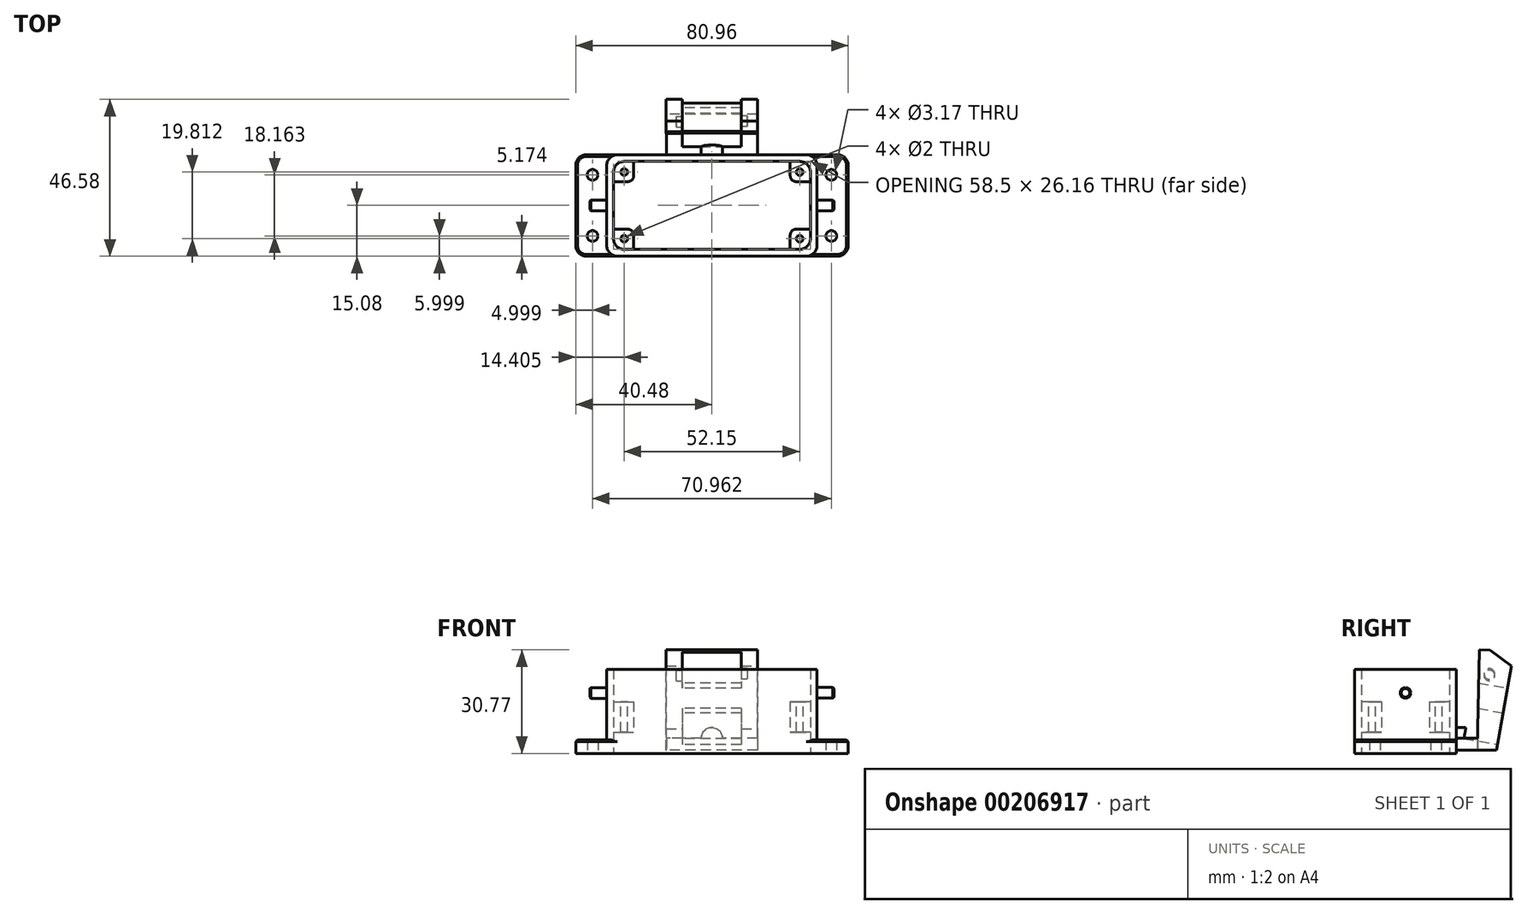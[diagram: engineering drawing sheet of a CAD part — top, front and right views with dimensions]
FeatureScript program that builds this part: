
annotation { "Feature Type Name" : "Feature", "Feature Type Description" : "" }
export const myFeature = defineFeature(function(context is Context, id is Id, definition is map)
    precondition{}
    {
        {
            var Q0;
            Q0=qCreatedBy(makeId("Top.planeOp"),FACE);
            var sketch = newSketch(context, id + "F0", { "sketchPlane" : qUnion([Q0])});
            skLineSegment(sketch, "E0.bottom", {"start": v(-37.3, 15.08) * mm, "end": v(37.3, 15.08) * mm});
            skLineSegment(sketch, "E0.top", {"start": v(-37.3, -15.08) * mm, "end": v(37.3, -15.08) * mm});
            skLineSegment(sketch, "E0.left", {"start": v(-40.48, 11.9) * mm, "end": v(-40.48, -11.9) * mm});
            skLineSegment(sketch, "E0.right", {"start": v(40.48, 11.9) * mm, "end": v(40.48, -11.9) * mm});
            skPoint(sketch, "E0.middle", {"position": v(0, 0) * mm});
            skCircle(sketch, "E1", {"center": v(-35.48, 9.08) * mm, "radius": 1.59 * mm});
            skCircle(sketch, "E2", {"center": v(-35.48, -9.08) * mm, "radius": 1.59 * mm});
            skCircle(sketch, "E3", {"center": v(35.48, -9.08) * mm, "radius": 1.59 * mm});
            skCircle(sketch, "E4", {"center": v(35.48, 9.08) * mm, "radius": 1.59 * mm});
            skPoint(sketch, "E5.visualSharp", {"position": v(-40.48, 15.08) * mm});
            skArc(sketch, "E5.filletArc", {"start": v(-37.3, 15.08) * mm, "mid": v(-39.55, 14.15) * mm, "end": v(-40.48, 11.9) * mm});
            skPoint(sketch, "E6.visualSharp", {"position": v(-40.48, -15.08) * mm});
            skArc(sketch, "E6.filletArc", {"start": v(-40.48, -11.9) * mm, "mid": v(-39.55, -14.15) * mm, "end": v(-37.3, -15.08) * mm});
            skPoint(sketch, "E7.visualSharp", {"position": v(40.48, -15.08) * mm});
            skArc(sketch, "E7.filletArc", {"start": v(37.3, -15.08) * mm, "mid": v(39.55, -14.15) * mm, "end": v(40.48, -11.9) * mm});
            skPoint(sketch, "E8.visualSharp", {"position": v(40.48, 15.08) * mm});
            skArc(sketch, "E8.filletArc", {"start": v(40.48, 11.9) * mm, "mid": v(39.55, 14.15) * mm, "end": v(37.3, 15.08) * mm});
            skLineSegment(sketch, "E9.bottom", {"start": v(-26.07, 13.08) * mm, "end": v(26.07, 13.08) * mm});
            skLineSegment(sketch, "E9.top", {"start": v(-26.07, -13.08) * mm, "end": v(26.07, -13.08) * mm});
            skLineSegment(sketch, "E9.left", {"start": v(-29.25, 9.9) * mm, "end": v(-29.25, -9.9) * mm});
            skLineSegment(sketch, "E9.right", {"start": v(29.25, 9.9) * mm, "end": v(29.25, -9.9) * mm});
            skPoint(sketch, "E10.visualSharp", {"position": v(-29.25, 13.08) * mm});
            skArc(sketch, "E10.filletArc", {"start": v(-26.07, 13.08) * mm, "mid": v(-28.32, 12.15) * mm, "end": v(-29.25, 9.9) * mm});
            skPoint(sketch, "E11.visualSharp", {"position": v(-29.25, -13.08) * mm});
            skArc(sketch, "E11.filletArc", {"start": v(-29.25, -9.9) * mm, "mid": v(-28.32, -12.15) * mm, "end": v(-26.07, -13.08) * mm});
            skPoint(sketch, "E12.visualSharp", {"position": v(29.25, -13.08) * mm});
            skArc(sketch, "E12.filletArc", {"start": v(26.07, -13.08) * mm, "mid": v(28.32, -12.15) * mm, "end": v(29.25, -9.9) * mm});
            skPoint(sketch, "E13.visualSharp", {"position": v(29.25, 13.08) * mm});
            skArc(sketch, "E13.filletArc", {"start": v(29.25, 9.9) * mm, "mid": v(28.32, 12.15) * mm, "end": v(26.07, 13.08) * mm});
            skSolve(sketch);
        }
        {
            var Q0;
            Q0=qSketchRegion(id+"F0",true);
            extrude(context, id + "F1", {"entities" : qUnion([Q0]), "depth" : 4 * mm});
        }
        {
            var Q0;
            Q0=makeQuery(id+"F1.opExtrude","CAP_FACE",FACE,{"disambiguationData":[OSD([sQuery(id+"F0.wireOp",EDGE,"E0.bottom"),sQuery(id+"F0.wireOp",EDGE,"E0.top"),sQuery(id+"F0.wireOp",EDGE,"E0.left"),sQuery(id+"F0.wireOp",EDGE,"E0.right"),sQuery(id+"F0.wireOp",EDGE,"E1"),sQuery(id+"F0.wireOp",EDGE,"E2"),sQuery(id+"F0.wireOp",EDGE,"E3"),sQuery(id+"F0.wireOp",EDGE,"E4"),sQuery(id+"F0.wireOp",EDGE,"E5.filletArc"),sQuery(id+"F0.wireOp",EDGE,"E6.filletArc"),sQuery(id+"F0.wireOp",EDGE,"E7.filletArc"),sQuery(id+"F0.wireOp",EDGE,"E8.filletArc"),sQuery(id+"F0.wireOp",EDGE,"E9.bottom"),sQuery(id+"F0.wireOp",EDGE,"E9.top"),sQuery(id+"F0.wireOp",EDGE,"E9.left"),sQuery(id+"F0.wireOp",EDGE,"E9.right"),sQuery(id+"F0.wireOp",EDGE,"E10.filletArc"),sQuery(id+"F0.wireOp",EDGE,"E11.filletArc"),sQuery(id+"F0.wireOp",EDGE,"E12.filletArc"),sQuery(id+"F0.wireOp",EDGE,"E13.filletArc")])],"isStart":false});
            var sketch = newSketch(context, id + "F2", { "sketchPlane" : qUnion([Q0])});
            skLineSegment(sketch, "E14.bottom", {"start": v(-26.07, 13.08) * mm, "end": v(26.07, 13.08) * mm});
            skLineSegment(sketch, "E14.top", {"start": v(-26.07, -13.08) * mm, "end": v(26.07, -13.08) * mm});
            skLineSegment(sketch, "E14.left", {"start": v(-29.25, 9.9) * mm, "end": v(-29.25, -9.9) * mm});
            skLineSegment(sketch, "E14.right", {"start": v(29.25, 9.9) * mm, "end": v(29.25, -9.9) * mm});
            skPoint(sketch, "E14.middle", {"position": v(0, 0) * mm});
            skPoint(sketch, "E15.visualSharp", {"position": v(-29.25, 13.08) * mm});
            skArc(sketch, "E15.filletArc", {"start": v(-26.07, 13.08) * mm, "mid": v(-28.32, 12.15) * mm, "end": v(-29.25, 9.9) * mm});
            skPoint(sketch, "E16.visualSharp", {"position": v(-29.25, -13.08) * mm});
            skArc(sketch, "E16.filletArc", {"start": v(-29.25, -9.9) * mm, "mid": v(-28.32, -12.15) * mm, "end": v(-26.07, -13.08) * mm});
            skPoint(sketch, "E17.visualSharp", {"position": v(29.25, -13.08) * mm});
            skArc(sketch, "E17.filletArc", {"start": v(26.07, -13.08) * mm, "mid": v(28.32, -12.15) * mm, "end": v(29.25, -9.9) * mm});
            skPoint(sketch, "E18.visualSharp", {"position": v(29.25, 13.08) * mm});
            skArc(sketch, "E18.filletArc", {"start": v(29.25, 9.9) * mm, "mid": v(28.32, 12.15) * mm, "end": v(26.07, 13.08) * mm});
            skLineSegment(sketch, "E19.bottom", {"start": v(-28.08, 15.08) * mm, "end": v(28.08, 15.08) * mm});
            skLineSegment(sketch, "E19.top", {"start": v(-28.08, -15.08) * mm, "end": v(28.08, -15.08) * mm});
            skLineSegment(sketch, "E19.left", {"start": v(-31.25, 11.9) * mm, "end": v(-31.25, -11.9) * mm});
            skLineSegment(sketch, "E19.right", {"start": v(31.25, 11.9) * mm, "end": v(31.25, -11.9) * mm});
            skPoint(sketch, "E20.visualSharp", {"position": v(-31.25, 15.08) * mm});
            skArc(sketch, "E20.filletArc", {"start": v(-28.08, 15.08) * mm, "mid": v(-30.32, 14.15) * mm, "end": v(-31.25, 11.9) * mm});
            skPoint(sketch, "E21.visualSharp", {"position": v(-31.25, -15.08) * mm});
            skArc(sketch, "E21.filletArc", {"start": v(-31.25, -11.9) * mm, "mid": v(-30.32, -14.15) * mm, "end": v(-28.08, -15.08) * mm});
            skPoint(sketch, "E22.visualSharp", {"position": v(31.25, -15.08) * mm});
            skArc(sketch, "E22.filletArc", {"start": v(28.08, -15.08) * mm, "mid": v(30.32, -14.15) * mm, "end": v(31.25, -11.9) * mm});
            skPoint(sketch, "E23.visualSharp", {"position": v(31.25, 15.08) * mm});
            skArc(sketch, "E23.filletArc", {"start": v(31.25, 11.9) * mm, "mid": v(30.32, 14.15) * mm, "end": v(28.08, 15.08) * mm});
            skSolve(sketch);
        }
        {
            var Q0;
            Q0=qSketchRegion(id+"F2",true);
            extrude(context, id + "F3", {"entities" : qUnion([Q0]), "operationType" : NewBodyOperationType.ADD, "depth" : 21 * mm});
        }
        {
            var Q0;
            {var subQ0=sQuery(id+"F0.wireOp",EDGE,"E7.filletArc");var subQ1=sQuery(id+"F0.wireOp",EDGE,"E0.top");Q0=makeQuery(id+"F3.boolean.opBoolean","SPLIT",EDGE,{"disambiguationData":[TD([makeQuery(id+"F1.opExtrude","SWEPT_FACE",FACE,{"disambiguationData":[OSD([subQ0])]})])],"derivedFrom":makeQuery(id+"F1.opExtrude","CAP_EDGE",EDGE,{"disambiguationData":[OSD([subQ1])],"isStart":false})});}
            var Q1;
            Q1=makeQuery(id+"F1.opExtrude","CAP_EDGE",EDGE,{"disambiguationData":[OSD([sQuery(id+"F0.wireOp",EDGE,"E7.filletArc")])],"isStart":false});
            var Q2;
            Q2=makeQuery(id+"F1.opExtrude","CAP_EDGE",EDGE,{"disambiguationData":[OSD([sQuery(id+"F0.wireOp",EDGE,"E0.right")])],"isStart":false});
            var Q3;
            Q3=makeQuery(id+"F1.opExtrude","CAP_EDGE",EDGE,{"disambiguationData":[OSD([sQuery(id+"F0.wireOp",EDGE,"E8.filletArc")])],"isStart":false});
            var Q4;
            {var subQ0=sQuery(id+"F0.wireOp",EDGE,"E8.filletArc");var subQ1=sQuery(id+"F0.wireOp",EDGE,"E0.bottom");Q4=makeQuery(id+"F3.boolean.opBoolean","SPLIT",EDGE,{"disambiguationData":[TD([makeQuery(id+"F1.opExtrude","SWEPT_FACE",FACE,{"disambiguationData":[OSD([subQ0])]})])],"derivedFrom":makeQuery(id+"F1.opExtrude","CAP_EDGE",EDGE,{"disambiguationData":[OSD([subQ1])],"isStart":false})});}
            var Q5;
            {var subQ0=sQuery(id+"F0.wireOp",EDGE,"E6.filletArc");var subQ1=sQuery(id+"F0.wireOp",EDGE,"E0.top");Q5=makeQuery(id+"F3.boolean.opBoolean","SPLIT",EDGE,{"disambiguationData":[TD([makeQuery(id+"F1.opExtrude","SWEPT_FACE",FACE,{"disambiguationData":[OSD([subQ0])]})])],"derivedFrom":makeQuery(id+"F1.opExtrude","CAP_EDGE",EDGE,{"disambiguationData":[OSD([subQ1])],"isStart":false})});}
            var Q6;
            Q6=makeQuery(id+"F1.opExtrude","CAP_EDGE",EDGE,{"disambiguationData":[OSD([sQuery(id+"F0.wireOp",EDGE,"E6.filletArc")])],"isStart":false});
            var Q7;
            Q7=makeQuery(id+"F1.opExtrude","CAP_EDGE",EDGE,{"disambiguationData":[OSD([sQuery(id+"F0.wireOp",EDGE,"E0.left")])],"isStart":false});
            var Q8;
            Q8=makeQuery(id+"F1.opExtrude","CAP_EDGE",EDGE,{"disambiguationData":[OSD([sQuery(id+"F0.wireOp",EDGE,"E5.filletArc")])],"isStart":false});
            var Q9;
            {var subQ0=sQuery(id+"F0.wireOp",EDGE,"E5.filletArc");var subQ1=sQuery(id+"F0.wireOp",EDGE,"E0.bottom");Q9=makeQuery(id+"F3.boolean.opBoolean","SPLIT",EDGE,{"disambiguationData":[TD([makeQuery(id+"F1.opExtrude","SWEPT_FACE",FACE,{"disambiguationData":[OSD([subQ0])]})])],"derivedFrom":makeQuery(id+"F1.opExtrude","CAP_EDGE",EDGE,{"disambiguationData":[OSD([subQ1])],"isStart":false})});}
            chamfer(context, id + "F4", {"entities" : qUnion([Q0, Q1, Q2, Q3, Q4, Q5, Q6, Q7, Q8, Q9]), "width" : 0.5 * mm, "tangentPropagation" : true});
        }
        {
            var Q0;
            Q0=makeQuery(id+"F3.opExtrude","SWEPT_FACE",FACE,{"disambiguationData":[OSD([sQuery(id+"F2.wireOp",EDGE,"E19.right")])]});
            var sketch = newSketch(context, id + "F5", { "sketchPlane" : qUnion([Q0])});
            skCircle(sketch, "E24", {"center": v(0, 18) * mm, "radius": 1.59 * mm});
            skSolve(sketch);
        }
        {
            var Q0;
            Q0=qSketchRegion(id+"F5",true);
            extrude(context, id + "F6", {"entities" : qUnion([Q0]), "operationType" : NewBodyOperationType.ADD, "depth" : 5 * mm});
        }
        {
            var Q0;
            Q0=makeQuery(id+"F3.opExtrude","SWEPT_FACE",FACE,{"disambiguationData":[OSD([sQuery(id+"F2.wireOp",EDGE,"E19.left")])]});
            var sketch = newSketch(context, id + "F7", { "sketchPlane" : qUnion([Q0])});
            skCircle(sketch, "E25", {"center": v(0, 17.99) * mm, "radius": 1.59 * mm});
            skSolve(sketch);
        }
        {
            var Q0;
            Q0=qSketchRegion(id+"F7",true);
            extrude(context, id + "F8", {"entities" : qUnion([Q0]), "operationType" : NewBodyOperationType.ADD, "depth" : 5 * mm});
        }
        {
            var Q0;
            Q0=makeQuery(id+"F6.opExtrude","CAP_EDGE",EDGE,{"disambiguationData":[OSD([sQuery(id+"F5.wireOp",EDGE,"E24")])],"isStart":false});
            var Q1;
            Q1=makeQuery(id+"F8.opExtrude","CAP_EDGE",EDGE,{"disambiguationData":[OSD([sQuery(id+"F7.wireOp",EDGE,"E25")])],"isStart":false});
            chamfer(context, id + "F9", {"entities" : qUnion([Q0, Q1]), "width" : 0.32 * mm, "tangentPropagation" : true});
        }
        {
            var Q0;
            Q0=qCreatedBy(makeId("Top.planeOp"),FACE);
            cPlane(context, id + "F10", {"entities" : qUnion([Q0]), "cplaneType" : CPlaneType.OFFSET, "offset" : 6.35 * mm, "width" : 152.4 * mm, "height" : 152.4 * mm});
        }
        {
            var Q0;
            Q0=qCreatedBy(id+"F10.planeOp",FACE);
            var sketch = newSketch(context, id + "F11", { "sketchPlane" : qUnion([Q0])});
            skLineSegment(sketch, "E26.bottom", {"start": v(-29.25, 7.08) * mm, "end": v(-24.96, 7.08) * mm});
            skLineSegment(sketch, "E26.top", {"start": v(-29.25, 13.08) * mm, "end": v(-23.25, 13.08) * mm});
            skLineSegment(sketch, "E26.left", {"start": v(-29.25, 7.08) * mm, "end": v(-29.25, 13.08) * mm});
            skLineSegment(sketch, "E26.right", {"start": v(-23.25, 8.8) * mm, "end": v(-23.25, 13.08) * mm});
            skLineSegment(sketch, "E27.bottom", {"start": v(-24.96, -7.08) * mm, "end": v(-29.25, -7.08) * mm});
            skLineSegment(sketch, "E27.top", {"start": v(-23.25, -13.08) * mm, "end": v(-29.25, -13.08) * mm});
            skLineSegment(sketch, "E27.left", {"start": v(-23.25, -8.8) * mm, "end": v(-23.25, -13.08) * mm});
            skLineSegment(sketch, "E27.right", {"start": v(-29.25, -7.08) * mm, "end": v(-29.25, -13.08) * mm});
            skLineSegment(sketch, "E28.bottom", {"start": v(24.96, -7.08) * mm, "end": v(29.25, -7.08) * mm});
            skLineSegment(sketch, "E28.top", {"start": v(23.25, -13.08) * mm, "end": v(29.25, -13.08) * mm});
            skLineSegment(sketch, "E28.left", {"start": v(23.25, -8.8) * mm, "end": v(23.25, -13.08) * mm});
            skLineSegment(sketch, "E28.right", {"start": v(29.25, -7.08) * mm, "end": v(29.25, -13.08) * mm});
            skLineSegment(sketch, "E29.bottom", {"start": v(24.96, 7.08) * mm, "end": v(29.25, 7.08) * mm});
            skLineSegment(sketch, "E29.top", {"start": v(23.25, 13.08) * mm, "end": v(29.25, 13.08) * mm});
            skLineSegment(sketch, "E29.left", {"start": v(23.25, 8.8) * mm, "end": v(23.25, 13.08) * mm});
            skLineSegment(sketch, "E29.right", {"start": v(29.25, 7.08) * mm, "end": v(29.25, 13.08) * mm});
            skPoint(sketch, "E30.visualSharp", {"position": v(-23.25, 7.08) * mm});
            skArc(sketch, "E30.filletArc", {"start": v(-24.96, 7.08) * mm, "mid": v(-23.75, 7.58) * mm, "end": v(-23.25, 8.8) * mm});
            skPoint(sketch, "E31.visualSharp", {"position": v(-23.25, -7.08) * mm});
            skArc(sketch, "E31.filletArc", {"start": v(-23.25, -8.8) * mm, "mid": v(-23.75, -7.58) * mm, "end": v(-24.96, -7.08) * mm});
            skPoint(sketch, "E32.visualSharp", {"position": v(23.25, -7.08) * mm});
            skArc(sketch, "E32.filletArc", {"start": v(24.96, -7.08) * mm, "mid": v(23.75, -7.58) * mm, "end": v(23.25, -8.8) * mm});
            skPoint(sketch, "E33.visualSharp", {"position": v(23.25, 7.08) * mm});
            skArc(sketch, "E33.filletArc", {"start": v(23.25, 8.8) * mm, "mid": v(23.75, 7.58) * mm, "end": v(24.96, 7.08) * mm});
            skSolve(sketch);
        }
        {
            var Q0;
            Q0=qSketchRegion(id+"F11",true);
            extrude(context, id + "F12", {"entities" : qUnion([Q0]), "operationType" : NewBodyOperationType.ADD, "depth" : 9 * mm});
        }
        {
            var Q0;
            Q0=makeQuery(id+"F12.opExtrude","CAP_FACE",FACE,{"disambiguationData":[OSD([sQuery(id+"F11.wireOp",EDGE,"E26.bottom"),sQuery(id+"F11.wireOp",EDGE,"E26.top"),sQuery(id+"F11.wireOp",EDGE,"E26.left"),sQuery(id+"F11.wireOp",EDGE,"E26.right"),sQuery(id+"F11.wireOp",EDGE,"E30.filletArc")])],"isStart":false});
            var sketch = newSketch(context, id + "F13", { "sketchPlane" : qUnion([Q0])});
            skPoint(sketch, "E34", {"position": v(-26.07, 9.9) * mm});
            skSolve(sketch);
        }
        {
            var Q0;
            Q0=makeQuery(id+"F12.opExtrude","CAP_FACE",FACE,{"disambiguationData":[OSD([sQuery(id+"F11.wireOp",EDGE,"E27.bottom"),sQuery(id+"F11.wireOp",EDGE,"E27.top"),sQuery(id+"F11.wireOp",EDGE,"E27.left"),sQuery(id+"F11.wireOp",EDGE,"E27.right"),sQuery(id+"F11.wireOp",EDGE,"E31.filletArc")])],"isStart":false});
            var sketch = newSketch(context, id + "F14", { "sketchPlane" : qUnion([Q0])});
            skPoint(sketch, "E35", {"position": v(-26.07, -9.9) * mm});
            skSolve(sketch);
        }
        {
            var Q0;
            Q0=makeQuery(id+"F12.opExtrude","CAP_FACE",FACE,{"disambiguationData":[OSD([sQuery(id+"F11.wireOp",EDGE,"E29.bottom"),sQuery(id+"F11.wireOp",EDGE,"E29.top"),sQuery(id+"F11.wireOp",EDGE,"E29.left"),sQuery(id+"F11.wireOp",EDGE,"E29.right"),sQuery(id+"F11.wireOp",EDGE,"E33.filletArc")])],"isStart":false});
            var sketch = newSketch(context, id + "F15", { "sketchPlane" : qUnion([Q0])});
            skPoint(sketch, "E36", {"position": v(26.07, 9.9) * mm});
            skSolve(sketch);
        }
        {
            var Q0;
            Q0=makeQuery(id+"F12.opExtrude","CAP_FACE",FACE,{"disambiguationData":[OSD([sQuery(id+"F11.wireOp",EDGE,"E28.bottom"),sQuery(id+"F11.wireOp",EDGE,"E28.top"),sQuery(id+"F11.wireOp",EDGE,"E28.left"),sQuery(id+"F11.wireOp",EDGE,"E28.right"),sQuery(id+"F11.wireOp",EDGE,"E32.filletArc")])],"isStart":false});
            var sketch = newSketch(context, id + "F16", { "sketchPlane" : qUnion([Q0])});
            skPoint(sketch, "E37", {"position": v(26.07, -9.9) * mm});
            skSolve(sketch);
        }
        {
            var Q0;
            Q0=sQuery(id+"F13.wireOp",VERTEX,"E34");
            var Q1;
            Q1=sQuery(id+"F14.wireOp",VERTEX,"E35");
            var Q2;
            Q2=sQuery(id+"F16.wireOp",VERTEX,"E37");
            var Q3;
            Q3=sQuery(id+"F15.wireOp",VERTEX,"E36");
            var Q4;
            Q4=makeQuery(id+"F1.opExtrude","SWEPT_BODY",BODY,{"disambiguationData":[OSD([sQuery(id+"F0.wireOp",EDGE,"E0.bottom"),sQuery(id+"F0.wireOp",EDGE,"E0.top"),sQuery(id+"F0.wireOp",EDGE,"E0.left"),sQuery(id+"F0.wireOp",EDGE,"E0.right"),sQuery(id+"F0.wireOp",EDGE,"E1"),sQuery(id+"F0.wireOp",EDGE,"E2"),sQuery(id+"F0.wireOp",EDGE,"E3"),sQuery(id+"F0.wireOp",EDGE,"E4"),sQuery(id+"F0.wireOp",EDGE,"E5.filletArc"),sQuery(id+"F0.wireOp",EDGE,"E6.filletArc"),sQuery(id+"F0.wireOp",EDGE,"E7.filletArc"),sQuery(id+"F0.wireOp",EDGE,"E8.filletArc"),sQuery(id+"F0.wireOp",EDGE,"E9.bottom"),sQuery(id+"F0.wireOp",EDGE,"E9.top"),sQuery(id+"F0.wireOp",EDGE,"E9.left"),sQuery(id+"F0.wireOp",EDGE,"E9.right"),sQuery(id+"F0.wireOp",EDGE,"E10.filletArc"),sQuery(id+"F0.wireOp",EDGE,"E11.filletArc"),sQuery(id+"F0.wireOp",EDGE,"E12.filletArc"),sQuery(id+"F0.wireOp",EDGE,"E13.filletArc")])]});
            hole(context, id + "F17", {"style" : HoleStyle.SIMPLE, "endStyle" : HoleEndStyle.THROUGH, "holeDiameter" : 2 * mm, "locations" : qUnion([Q0, Q1, Q2, Q3]), "scope" : qUnion([Q4]), "isTappedThrough" : true});
        }
        {
            var Q0;
            Q0=makeQuery(id+"F3.boolean.opBoolean","MERGE",FACE,{"derivedFrom":[makeQuery(id+"F1.opExtrude","SWEPT_FACE",FACE,{"disambiguationData":[OSD([sQuery(id+"F0.wireOp",EDGE,"E0.bottom")])]}),makeQuery(id+"F3.opExtrude","SWEPT_FACE",FACE,{"disambiguationData":[OSD([sQuery(id+"F2.wireOp",EDGE,"E19.bottom")])]})]});
            var sketch = newSketch(context, id + "F18", { "sketchPlane" : qUnion([Q0])});
            skLineSegment(sketch, "E38.bottom", {"start": v(-13.5, 4.5) * mm, "end": v(-3.17, 4.5) * mm});
            skLineSegment(sketch, "E38.top", {"start": v(-13.5, 1) * mm, "end": v(13.5, 1) * mm});
            skLineSegment(sketch, "E38.left", {"start": v(-13.5, 4.5) * mm, "end": v(-13.5, 1) * mm});
            skLineSegment(sketch, "E38.right", {"start": v(13.5, 4.5) * mm, "end": v(13.5, 1) * mm});
            skArc(sketch, "E39", {"start": v(3.18, 4.5) * mm, "mid": v(0, 7.67) * mm, "end": v(-3.17, 4.5) * mm});
            skLineSegment(sketch, "E40.trimOffspring", {"start": v(3.18, 4.5) * mm, "end": v(13.5, 4.5) * mm});
            skSolve(sketch);
        }
        {
            var Q0;
            Q0=qSketchRegion(id+"F18",true);
            extrude(context, id + "F19", {"entities" : qUnion([Q0]), "operationType" : NewBodyOperationType.ADD, "depth" : 12 * mm});
        }
        {
            var Q0;
            Q0=makeQuery(id+"F19.opExtrude","SWEPT_FACE",FACE,{"disambiguationData":[OSD([sQuery(id+"F18.wireOp",EDGE,"E38.left")])]});
            var sketch = newSketch(context, id + "F20", { "sketchPlane" : qUnion([Q0])});
            skLineSegment(sketch, "E41", {"start": v(21.43, 1) * mm, "end": v(21.43, 7.35) * mm});
            skLineSegment(sketch, "E42", {"start": v(21.43, 7.35) * mm, "end": v(21.92, 30.77) * mm});
            skLineSegment(sketch, "E43", {"start": v(21.92, 30.77) * mm, "end": v(25.1, 30.7) * mm});
            skLineSegment(sketch, "E44", {"start": v(25.1, 30.7) * mm, "end": v(31.5, 26.01) * mm});
            skLineSegment(sketch, "E45", {"start": v(31.5, 26.01) * mm, "end": v(27.09, 1) * mm});
            skLineSegment(sketch, "E46", {"start": v(27.09, 1) * mm, "end": v(21.43, 1) * mm});
            skSolve(sketch);
        }
        {
            var Q0;
            Q0=qSketchRegion(id+"F20",true);
            extrude(context, id + "F21", {"entities" : qUnion([Q0]), "operationType" : NewBodyOperationType.ADD, "oppositeDirection" : true, "depth" : 27.1 * mm});
        }
        {
            var Q0;
            Q0=makeQuery(id+"F21.opExtrude","SWEPT_FACE",FACE,{"disambiguationData":[OSD([sQuery(id+"F20.wireOp",EDGE,"E45")])]});
            var sketch = newSketch(context, id + "F22", { "sketchPlane" : qUnion([Q0])});
            skLineSegment(sketch, "E47.bottom", {"start": v(-8.73, 16.93) * mm, "end": v(8.86, 16.93) * mm});
            skLineSegment(sketch, "E47.top", {"start": v(-8.73, 7.4) * mm, "end": v(8.86, 7.4) * mm});
            skLineSegment(sketch, "E47.left", {"start": v(-8.73, 16.93) * mm, "end": v(-8.73, 7.4) * mm});
            skLineSegment(sketch, "E47.right", {"start": v(8.86, 16.93) * mm, "end": v(8.86, 7.4) * mm});
            skLineSegment(sketch, "E48", {"start": v(-8.73, 37.12) * mm, "end": v(-8.73, 24.42) * mm});
            skLineSegment(sketch, "E49", {"start": v(-8.73, 24.42) * mm, "end": v(8.86, 24.42) * mm});
            skLineSegment(sketch, "E50", {"start": v(8.86, 24.42) * mm, "end": v(8.86, 37.12) * mm});
            skLineSegment(sketch, "E51", {"start": v(8.86, 37.12) * mm, "end": v(-8.73, 37.12) * mm});
            skSolve(sketch);
        }
        {
            var Q0;
            Q0=qSketchRegion(id+"F22",true);
            extrude(context, id + "F23", {"entities" : qUnion([Q0]), "operationType" : NewBodyOperationType.REMOVE, "oppositeDirection" : true, "depth" : 10.16 * mm});
        }
        {
            var Q0;
            Q0=makeQuery(id+"F23.boolean.opBoolean","COPY",FACE,{"derivedFrom":makeQuery(id+"F23.opExtrude","SWEPT_FACE",FACE,{"disambiguationData":[OSD([sQuery(id+"F22.wireOp",EDGE,"E50")])]})});
            var sketch = newSketch(context, id + "F24", { "sketchPlane" : qUnion([Q0])});
            skCircle(sketch, "E52", {"center": v(24.94, 23.2) * mm, "radius": 1.59 * mm});
            skSolve(sketch);
        }
        {
            var Q0;
            Q0=makeQuery(id+"F23.boolean.opBoolean","COPY",FACE,{"derivedFrom":makeQuery(id+"F23.opExtrude","SWEPT_FACE",FACE,{"disambiguationData":[OSD([sQuery(id+"F22.wireOp",EDGE,"E48")])]})});
            var sketch = newSketch(context, id + "F25", { "sketchPlane" : qUnion([Q0])});
            skCircle(sketch, "E53", {"center": v(-24.95, 23.62) * mm, "radius": 1.59 * mm});
            skSolve(sketch);
        }
        {
            var Q0;
            Q0=makeQuery(id+"F25.imprint","IMPRINT",FACE,{"disambiguationData":[TD([[makeQuery(id+"F25.imprint","IMPRINT",EDGE,{"derivedFrom":sQuery(id+"F25.wireOp",EDGE,"E53")}),1.0]])]});
            extrude(context, id + "F26", {"entities" : qUnion([Q0]), "operationType" : NewBodyOperationType.REMOVE, "oppositeDirection" : true, "depth" : 1.71 * mm});
        }
        {
            var Q0;
            Q0=makeQuery(id+"F24.imprint","IMPRINT",FACE,{"disambiguationData":[TD([[makeQuery(id+"F24.imprint","IMPRINT",EDGE,{"derivedFrom":sQuery(id+"F24.wireOp",EDGE,"E52")}),1.0]])]});
            extrude(context, id + "F27", {"entities" : qUnion([Q0]), "operationType" : NewBodyOperationType.REMOVE, "oppositeDirection" : true, "depth" : 1.71 * mm});
        }
    });
